# Revit family: Power-MouldedCaseDevices-GEWISS-97MSS-SWITCH_DISCONNECTOR_630_4P
name_source: partatom
category: Apparecchi elettrici
revit_build: Autodesk Revit 2016 (Build: 20161004_0715(x64)
units: mm (PartAtom-declared; Revit-internal decimal feet)

## family parameters
Condiviso = No
Host = Muro
Mantenere orientamento annotazione = Sì
Numero OmniClass = 23.80.50.00
Punto di calcolo locali = Sì
Quota connettore circolare = Usa diametro
Sempre verticale = Sì
Taglio con vuoti quando caricato = No
Tipo di parte = Normale
Titolo OmniClass = Terminals for Power Supply

## types (2) — shared parameters
Catalogue = POWER
Catalogue Range = 97 MSS
GW - Codice Electrocod = 150
IDF = 91573172-9ef6-4ff1-bd0e-2b967b27cf72
IDT = 5ccbb37a-71f1-4c7e-90c4-2e8808b06f3c
Immagine tipo = GW97734.jpg
Label = MSS 630
No. of poles = 4P
Number of poles = 4P
Produttore = GEWISS S.p.A.
Rated voltage = 400V
SEO = Disconnector
Technical sheet = https://www.gewiss.com
URL = https://www.gewiss.com
Version file RFA = 18.0

## per-type parameters (varying)
| type | Descrizione | EAN code | Modello | Rated current (In) | Rated current: |
| GW97733 - SWITCH DISCONNECTOR MSS 630 4P 400A | SWITCH DISCONNECTOR MSS 630 4P 400A | 8011564211537 | GW97733 | 400A | 400A |
| GW97734 - SWITCH DISCONNECTOR MSS 630 4P 630A | SWITCH DISCONNECTOR MSS 630 4P 630A | 8011564211544 | GW97734 | 630A | 630A |
